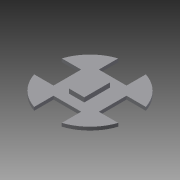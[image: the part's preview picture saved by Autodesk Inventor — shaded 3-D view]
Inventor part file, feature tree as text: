
AUTODESK INVENTOR PART (.ipt)
format: ipt  version: 2015 (Build 190159000, 159)  size: 120,832 bytes
history: native  units: in
note: dims shown in document units (in); Inventor stores cm internally (conversion verified against a paired STEP export)
features: other x3, sketch x2, extrude x1, pattern_circular x1
ambient origin geometry x8: Origin, YZ Plane, XZ Plane, XY Plane, X Axis, Y Axis, Z Axis, Center Point
bodies: Solid1 (feature_tree)
feature tree (7):
  other  "roundBase.ipt"
  sketch  "Sketch1"  dims[d0=0.1969in d1=1.0in d2=0.0in d3=1.5748in d4=360.0deg]
  extrude  "Extrusion1"  Depth=0.1969in TaperAngle=0.0deg
  pattern_circular  "Circular Pattern1"  Count=4 Angle=360.0deg
  other  "Solid1::roundBase.ipt"
  other  "TaggingFeature1"
  sketch  "Sketch2"
